# Revit family: P350211-009
name_source: partatom
category: Lighting Fixtures
units: mm (PartAtom-declared; Revit-internal decimal feet)

## family parameters
Cut with Voids When Loaded = No
Host = Face
Light Source = Yes
OmniClass Number = 23.80.70.11.14.11
OmniClass Title = Downlights
Part Type = Normal
Room Calculation Point = No
Round Connector Dimension = Use Diameter
Shared = No

## types (1)
- P710102-060-30
    Apparent Load = 10 VA
    Certifications = • cCSAus certified to UL 1598
• Wall Mount: Suitable for wet locations
• Surface & Pendant Mount: Suitable for wet
locations under covered ceiling
• Cord Mount and all Wall Wash: Suitable for
damp locations
    Color Filter = 16777215
    Default Elevation = 48 "
    Description = Curve LED One-Light White Opal Acrylic Modern Style Wall Sconce Light
    Dimming Lamp Color Temperature Shift = <None>
    Features = Bring a touch of contemporary design with the Curve LED Collection 1-Light Opal White Shade LED Modern Wall Light. The opal white shade designed with an arching acrylic shade is accented by two finals that add visual interest. Comes with a set of three finals for customization (matte black, brushed nickel, and architectural bronze).The light source glows from behind the curved shade to foster a contemporary glow.
Curve LED Collection 1-Light Modern Opal White Shade Sconce
Application: Bring a touch of contemporary design with the Curve LED Collection 1-Light Opal White Shade LED Modern Wall Light ideal for any entryway, hallway, foyer, bedroom, sitting room living room, or bathroom.
Styles: Perfect for contemporary and modern style settings.
Finish: The opal white shade designed with an arching acrylic shade is accented by two finals that add visual interest
comes with a set of three finals for customization (matte black, brushed nickel, and architectural bronze).
Materials: Constructed from steel to ensure a long product lifespan.
Glass/Shades: The light source glows from behind the curved shade to foster a contemporary glow.
Bulbs: For ideal illumination, 1 integrated LED is included (10w)
3000K
90CRI
744 delivered lumens
dimmable.
Dimensions: Measures 8-inch diameter by 8-inch height.
Certifications: cETLus damp location listed, meets California Title 24 JA8-2019.
Pairs With: Pairs with a variety of Progress Lighting fixtures.
    Glass = Glass - Hubbell - White
    Gold = Paint - Hubbell - White Texture
    Housing Material = Paint - Hubbell - White Texture
    Lamp = LED/CFL/incandescent
    Manufacturer = Progress Lighting
    Model = P710102-060-30
    Photometric Web File = PROG_P710102-060-30_20.00259_testlabreports.ies
    Product Documentation Link = https://hubbellcdn.com
    Product Page URL = https://www.hubbell.com
    Tilt Angle = 180.00°
    URL = https://www.hubbell.com
    Voltage = 120 V
    Warranty = 5 year warranty
    Wattage Comments = 10W

## geometry (parser evidence)
native form markers: Sweep x1
no freeform markers — native parametric forms only
